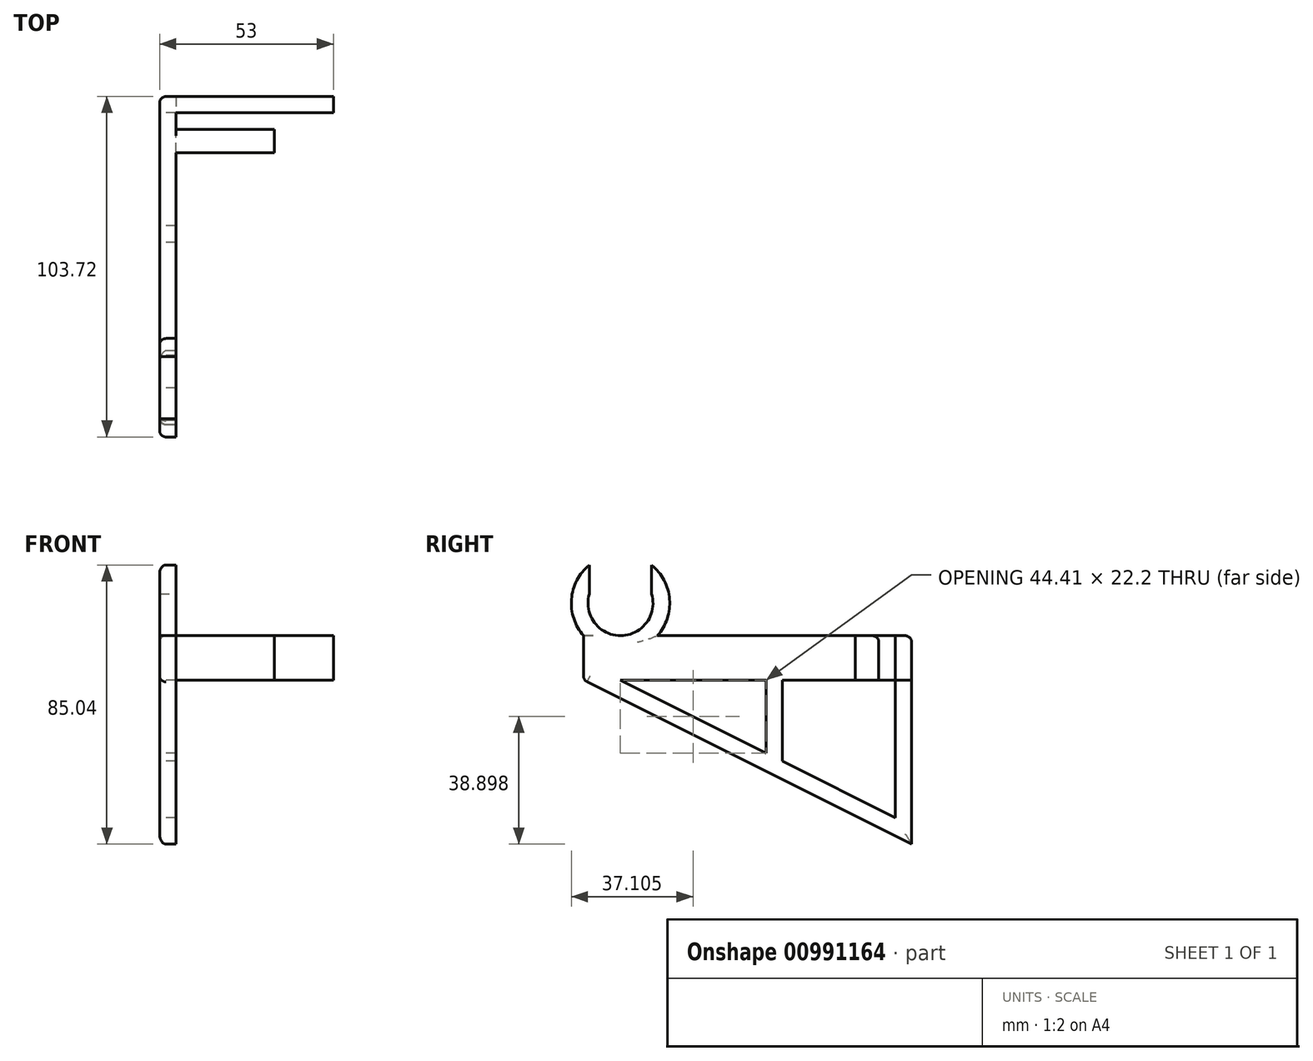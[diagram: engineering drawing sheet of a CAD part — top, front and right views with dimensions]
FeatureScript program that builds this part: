
annotation { "Feature Type Name" : "Feature", "Feature Type Description" : "" }
export const myFeature = defineFeature(function(context is Context, id is Id, definition is map)
    precondition{}
    {
        {
            var Q0;
            Q0=qCreatedBy(makeId("Top.planeOp"),FACE);
            var sketch = newSketch(context, id + "F0", { "sketchPlane" : qUnion([Q0])});
            skLineSegment(sketch, "E0", {"start": v(0, 0) * mm, "end": v(0, 5) * mm});
            skLineSegment(sketch, "E1", {"start": v(0, 5) * mm, "end": v(-53, 5) * mm});
            skLineSegment(sketch, "E2", {"start": v(-53, 5) * mm, "end": v(-53, -95) * mm});
            skLineSegment(sketch, "E3", {"start": v(-53, -95) * mm, "end": v(-48, -95) * mm});
            skLineSegment(sketch, "E4", {"start": v(-48, -95) * mm, "end": v(-48, 0) * mm});
            skLineSegment(sketch, "E5", {"start": v(-48, 0) * mm, "end": v(0, 0) * mm});
            skSolve(sketch);
        }
        {
            var Q0;
            Q0=makeQuery(id+"F0.imprint","IMPRINT",FACE,{"disambiguationData":[TD([[makeQuery(id+"F0.imprint","IMPRINT",EDGE,{"derivedFrom":sQuery(id+"F0.wireOp",EDGE,"E0")}),1.0]])]});
            extrude(context, id + "F1", {"entities" : qUnion([Q0]), "depth" : 13.5 * mm, "offsetDistance" : 25 * mm});
        }
        {
            var Q0;
            Q0=makeQuery(id+"F1.opExtrude","SWEPT_FACE",FACE,{"disambiguationData":[OSD([sQuery(id+"F0.wireOp",EDGE,"E2")])]});
            var sketch = newSketch(context, id + "F2", { "sketchPlane" : qUnion([Q0])});
            skLineSegment(sketch, "E6", {"start": v(-5, 0) * mm, "end": v(-5, -50) * mm});
            skLineSegment(sketch, "E7", {"start": v(-5, -50) * mm, "end": v(95, 0) * mm});
            skSolve(sketch);
        }
        {
            var Q0;
            Q0=makeQuery(id+"F2.imprint","IMPRINT",FACE,{"disambiguationData":[TD([[makeQuery(id+"F2.imprint","IMPRINT",EDGE,{"derivedFrom":sQuery(id+"F2.wireOp",EDGE,"E6")}),1.0]])]});
            extrude(context, id + "F3", {"entities" : qUnion([Q0]), "operationType" : NewBodyOperationType.ADD, "oppositeDirection" : true, "depth" : 5 * mm, "offsetDistance" : 25 * mm});
        }
        {
            var Q0;
            {var subQ0=sQuery(id+"F0.wireOp",EDGE,"E2");Q0=makeQuery(id+"F3.boolean.opBoolean","MERGE",FACE,{"derivedFrom":[makeQuery(id+"F1.opExtrude","SWEPT_FACE",FACE,{"disambiguationData":[OSD([subQ0])]}),makeQuery(id+"F3.opExtrude","CAP_FACE",FACE,{"disambiguationData":[OSD([subQ0,sQuery(id+"F2.wireOp",EDGE,"E6"),sQuery(id+"F2.wireOp",EDGE,"E7")])],"isStart":true})]});}
            var sketch = newSketch(context, id + "F4", { "sketchPlane" : qUnion([Q0])});
            skLineSegment(sketch, "E8", {"start": v(0, 0) * mm, "end": v(0, -41.9) * mm});
            skLineSegment(sketch, "E9", {"start": v(0, -41.9) * mm, "end": v(83.82, 0) * mm});
            skLineSegment(sketch, "E10", {"start": v(83.82, 0) * mm, "end": v(0, 0) * mm});
            skLineSegment(sketch, "E11", {"start": v(34.4, 0) * mm, "end": v(34.4, -24.7) * mm});
            skLineSegment(sketch, "E12", {"start": v(39.4, 0) * mm, "end": v(39.4, -22.2) * mm});
            skSolve(sketch);
        }
        {
            var Q0;
            Q0=makeQuery(id+"F4.imprint","IMPRINT",FACE,{"disambiguationData":[TD([[makeQuery(id+"F4.imprint","IMPRINT",EDGE,{"derivedFrom":sQuery(id+"F4.wireOp",EDGE,"E8")}),1.0]])]});
            var Q1;
            {var subQ3=sQuery(id+"F4.wireOp",EDGE,"E12");Q1=makeQuery(id+"F4.imprint","IMPRINT",FACE,{"disambiguationData":[TD([[makeQuery(id+"F4.imprint","IMPRINT",EDGE,{"derivedFrom":subQ3}),1.0]])]});}
            extrude(context, id + "F5", {"entities" : qUnion([Q0, Q1]), "operationType" : NewBodyOperationType.REMOVE, "endBound" : BoundingType.UP_TO_NEXT, "oppositeDirection" : true, "depth" : 25 * mm, "offsetDistance" : 25 * mm});
        }
        {
            var Q0;
            {var subQ0=sQuery(id+"F0.wireOp",EDGE,"E2");Q0=makeQuery(id+"F3.boolean.opBoolean","MERGE",FACE,{"derivedFrom":[makeQuery(id+"F1.opExtrude","SWEPT_FACE",FACE,{"disambiguationData":[OSD([subQ0])]}),makeQuery(id+"F3.opExtrude","CAP_FACE",FACE,{"disambiguationData":[OSD([subQ0,sQuery(id+"F2.wireOp",EDGE,"E6"),sQuery(id+"F2.wireOp",EDGE,"E7")])],"isStart":true})]});}
            var sketch = newSketch(context, id + "F6", { "sketchPlane" : qUnion([Q0])});
            skCircle(sketch, "E13", {"center": v(83.72, 23.43) * mm, "radius": 9.9 * mm});
            skCircle(sketch, "E14", {"center": v(83.72, 23.43) * mm, "radius": 15 * mm});
            skLineSegment(sketch, "E15", {"start": v(83.72, 23.43) * mm, "end": v(83.72, 42.88) * mm, "construction": true});
            skPoint(sketch, "E16.orphan", {"position": v(-36.4, 37.76) * mm});
            skSolve(sketch);
        }
        {
            var Q0;
            {var subQ0=sQuery(id+"F6.wireOp",EDGE,"E13");var subQ1=makeQuery(id+"F1.opExtrude","CAP_EDGE",EDGE,{"disambiguationData":[OSD([sQuery(id+"F0.wireOp",EDGE,"E2")])],"isStart":false});var subQ2=makeQuery(id+"F6.imprint","INTERSECT",VERTEX,{"disambiguationData":[OD(0.0)],"derivedFrom":[subQ1,subQ0]});Q0=makeQuery(id+"F6.imprint","IMPRINT",FACE,{"disambiguationData":[TD([[makeQuery(id+"F6.imprint","IMPRINT",EDGE,{"disambiguationData":[TD([[subQ2,1.0]])],"derivedFrom":subQ0}),-1.0]])]});}
            extrude(context, id + "F7", {"entities" : qUnion([Q0]), "operationType" : NewBodyOperationType.ADD, "oppositeDirection" : true, "depth" : 5 * mm, "offsetDistance" : 25 * mm});
        }
        {
            var Q0;
            {var subQ0=sQuery(id+"F0.wireOp",EDGE,"E2");Q0=makeQuery(id+"F7.boolean.opBoolean","MERGE",FACE,{"derivedFrom":[makeQuery(id+"F3.boolean.opBoolean","MERGE",FACE,{"derivedFrom":[makeQuery(id+"F1.opExtrude","SWEPT_FACE",FACE,{"disambiguationData":[OSD([sQuery(id+"F0.wireOp",EDGE,"E4")])]}),makeQuery(id+"F3.opExtrude","CAP_FACE",FACE,{"disambiguationData":[OSD([subQ0,sQuery(id+"F2.wireOp",EDGE,"E6"),sQuery(id+"F2.wireOp",EDGE,"E7")])],"isStart":false})]}),makeQuery(id+"F7.opExtrude","CAP_FACE",FACE,{"disambiguationData":[OSD([subQ0,sQuery(id+"F6.wireOp",EDGE,"E13"),sQuery(id+"F6.wireOp",EDGE,"E14")])],"isStart":false})]});}
            var sketch = newSketch(context, id + "F8", { "sketchPlane" : qUnion([Q0])});
            skLineSegment(sketch, "E17.bottom", {"start": v(-5, 0) * mm, "end": v(-12.16, 0) * mm});
            skLineSegment(sketch, "E17.top", {"start": v(-5, 13.5) * mm, "end": v(-12.16, 13.5) * mm});
            skLineSegment(sketch, "E17.left", {"start": v(-5, 0) * mm, "end": v(-5, 13.5) * mm});
            skLineSegment(sketch, "E17.right", {"start": v(-12.16, 0) * mm, "end": v(-12.16, 13.5) * mm});
            skSolve(sketch);
        }
        {
            var Q0;
            Q0=makeQuery(id+"F8.imprint","IMPRINT",FACE,{"disambiguationData":[TD([[makeQuery(id+"F8.imprint","IMPRINT",EDGE,{"derivedFrom":sQuery(id+"F8.wireOp",EDGE,"E17.bottom")}),-1.0]])]});
            extrude(context, id + "F9", {"entities" : qUnion([Q0]), "operationType" : NewBodyOperationType.ADD, "depth" : 30 * mm, "offsetDistance" : 25 * mm});
        }
        {
            var Q0;
            {var subQ0=sQuery(id+"F2.wireOp",EDGE,"E7");var subQ2=sQuery(id+"F0.wireOp",EDGE,"E4");var subQ3=makeQuery(id+"F1.opExtrude","SWEPT_FACE",FACE,{"disambiguationData":[OSD([subQ2])]});var subQ4=sQuery(id+"F2.wireOp",EDGE,"E6");var subQ5=sQuery(id+"F0.wireOp",EDGE,"E2");var subQ6=makeQuery(id+"F3.opExtrude","CAP_FACE",FACE,{"disambiguationData":[OSD([subQ5,subQ4,subQ0])],"isStart":false});var subQ8=sQuery(id+"F0.wireOp",EDGE,"E1");var subQ16=sQuery(id+"F6.wireOp",EDGE,"E13");var subQ17=sQuery(id+"F6.wireOp",EDGE,"E14");var subQ18=makeQuery(id+"F7.opExtrude","CAP_FACE",FACE,{"disambiguationData":[OSD([subQ5,subQ16,subQ17])],"isStart":false});Q0=makeQuery(id+"F9.boolean.opBoolean","SPLIT",FACE,{"disambiguationData":[TD([makeQuery(id+"F1.opExtrude","SWEPT_FACE",FACE,{"disambiguationData":[OSD([subQ8])]})])],"derivedFrom":makeQuery(id+"F7.boolean.opBoolean","MERGE",FACE,{"derivedFrom":[makeQuery(id+"F3.boolean.opBoolean","MERGE",FACE,{"derivedFrom":[subQ3,subQ6]}),subQ18]})});}
            var sketch = newSketch(context, id + "F10", { "sketchPlane" : qUnion([Q0])});
            skLineSegment(sketch, "E18", {"start": v(-83.72, 23.43) * mm, "end": v(-83.72, 51.9) * mm, "construction": true});
            skPoint(sketch, "E18.endSnap0", {"position": v(-83.72, 38.43) * mm});
            skLineSegment(sketch, "E19.bottom", {"start": v(-74.22, 23.52) * mm, "end": v(-93.22, 23.52) * mm});
            skLineSegment(sketch, "E19.top", {"start": v(-74.22, 53.34) * mm, "end": v(-93.22, 53.34) * mm});
            skLineSegment(sketch, "E19.left", {"start": v(-74.22, 23.52) * mm, "end": v(-74.22, 53.34) * mm});
            skLineSegment(sketch, "E19.right", {"start": v(-93.22, 23.52) * mm, "end": v(-93.22, 53.34) * mm});
            skSolve(sketch);
        }
        {
            var Q0;
            {var subQ0=sQuery(id+"F10.wireOp",EDGE,"E19.left");var subQ1=makeQuery(id+"F7.opExtrude","CAP_EDGE",EDGE,{"disambiguationData":[OSD([sQuery(id+"F6.wireOp",EDGE,"E14")])],"isStart":false});var subQ2=makeQuery(id+"F10.imprint","INTERSECT",VERTEX,{"derivedFrom":[subQ1,subQ0]});Q0=makeQuery(id+"F10.imprint","IMPRINT",FACE,{"disambiguationData":[TD([[makeQuery(id+"F10.imprint","IMPRINT",EDGE,{"disambiguationData":[TD([[subQ2,1.0]])],"derivedFrom":subQ0}),1.0]])]});}
            extrude(context, id + "F11", {"entities" : qUnion([Q0]), "operationType" : NewBodyOperationType.REMOVE, "endBound" : BoundingType.UP_TO_NEXT, "oppositeDirection" : true, "depth" : 25 * mm, "offsetDistance" : 25 * mm});
        }
        {
            var Q0;
            Q0=makeQuery(id+"F3.boolean.opBoolean","MERGE",EDGE,{"derivedFrom":[makeQuery(id+"F1.opExtrude","SWEPT_EDGE",EDGE,{"disambiguationData":[OSD([sQuery(id+"F0.wireOp",EDGE,"E1"),sQuery(id+"F0.wireOp",EDGE,"E2")])]}),makeQuery(id+"F3.opExtrude","CAP_EDGE",EDGE,{"disambiguationData":[OSD([sQuery(id+"F2.wireOp",EDGE,"E6")])],"isStart":true})]});
            var Q1;
            Q1=makeQuery(id+"F3.opExtrude","CAP_EDGE",EDGE,{"disambiguationData":[OSD([sQuery(id+"F2.wireOp",EDGE,"E7")])],"isStart":true});
            var Q2;
            {var subQ0=sQuery(id+"F6.wireOp",EDGE,"E14");Q2=makeQuery(id+"F11.boolean.opBoolean","SPLIT",EDGE,{"disambiguationData":[TD([makeQuery(id+"F11.opExtrude","SWEPT_FACE",FACE,{"disambiguationData":[OSD([sQuery(id+"F10.wireOp",EDGE,"E19.right")])]})])],"derivedFrom":makeQuery(id+"F7.opExtrude","CAP_EDGE",EDGE,{"disambiguationData":[OSD([subQ0])],"isStart":true})});}
            fillet(context, id + "F12", {"entities" : qUnion([Q0, Q1, Q2]), "radius" : 2 * mm, "tangentPropagation" : true, "allowEdgeOverflow" : false});
        }
        {
            var Q0;
            {var subQ0=sQuery(id+"F0.wireOp",EDGE,"E2");var subQ2=sQuery(id+"F0.wireOp",EDGE,"E1");Q0=makeQuery(id+"F7.boolean.opBoolean","SPLIT",EDGE,{"disambiguationData":[TD([makeQuery(id+"F1.opExtrude","SWEPT_FACE",FACE,{"disambiguationData":[OSD([subQ2])]})])],"derivedFrom":makeQuery(id+"F1.opExtrude","CAP_EDGE",EDGE,{"disambiguationData":[OSD([subQ0])],"isStart":false})});}
            var Q1;
            Q1=makeQuery(id+"F1.opExtrude","SWEPT_EDGE",EDGE,{"disambiguationData":[OSD([sQuery(id+"F0.wireOp",EDGE,"E2"),sQuery(id+"F0.wireOp",EDGE,"E3")])]});
            var Q2;
            {var subQ0=sQuery(id+"F6.wireOp",EDGE,"E14");Q2=makeQuery(id+"F11.boolean.opBoolean","SPLIT",EDGE,{"disambiguationData":[TD([makeQuery(id+"F9.opExtrude","SWEPT_FACE",FACE,{"disambiguationData":[OSD([sQuery(id+"F8.wireOp",EDGE,"E17.top")])]})])],"derivedFrom":makeQuery(id+"F7.opExtrude","CAP_EDGE",EDGE,{"disambiguationData":[OSD([subQ0])],"isStart":true})});}
            var Q3;
            Q3=makeQuery(id+"F9.opExtrude","SWEPT_EDGE",EDGE,{"disambiguationData":[OSD([sQuery(id+"F0.wireOp",EDGE,"E4"),sQuery(id+"F8.wireOp",EDGE,"E17.top"),sQuery(id+"F8.wireOp",EDGE,"E17.left")])]});
            fillet(context, id + "F13", {"entities" : qUnion([Q0, Q1, Q2, Q3]), "radius" : 2 * mm, "tangentPropagation" : true, "allowEdgeOverflow" : false});
        }
    });
